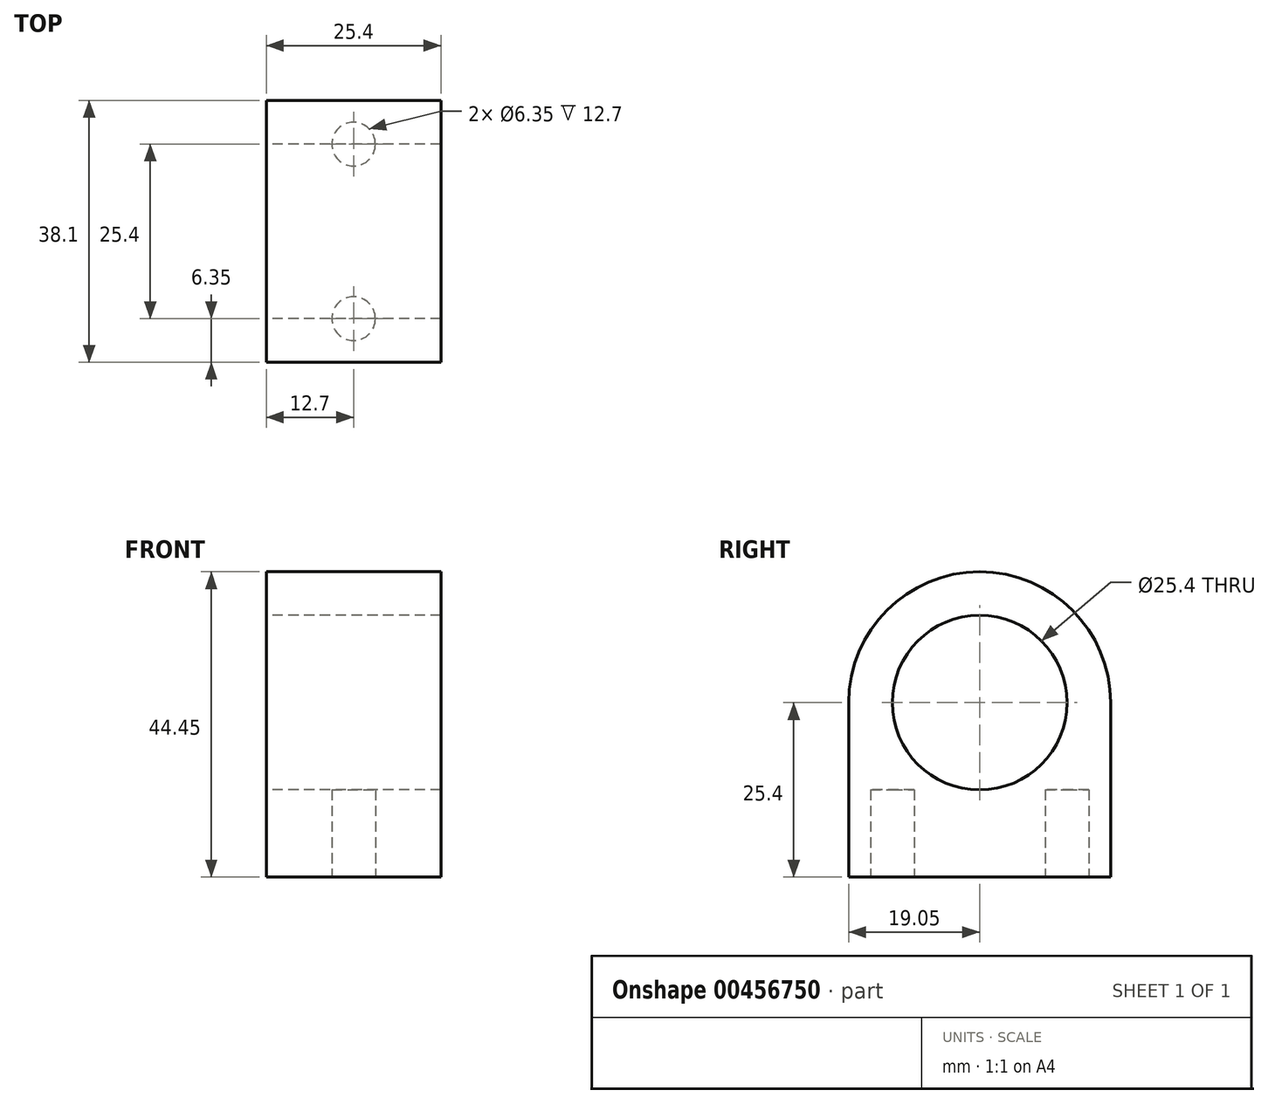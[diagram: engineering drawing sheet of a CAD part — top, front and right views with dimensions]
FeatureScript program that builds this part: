
annotation { "Feature Type Name" : "Feature", "Feature Type Description" : "" }
export const myFeature = defineFeature(function(context is Context, id is Id, definition is map)
    precondition{}
    {
        {
            var Q0;
            Q0=qCreatedBy(makeId("Right.planeOp"),FACE);
            var sketch = newSketch(context, id + "F0", { "sketchPlane" : qUnion([Q0])});
            skArc(sketch, "E0", {"start": v(19.05, 0) * mm, "mid": v(0, 19.05) * mm, "end": v(-19.05, 0) * mm});
            skCircle(sketch, "E1", {"center": v(0, 0) * mm, "radius": 12.7 * mm});
            skLineSegment(sketch, "E2", {"start": v(-19.05, 0) * mm, "end": v(-19.05, -25.4) * mm});
            skLineSegment(sketch, "E3", {"start": v(19.05, 0) * mm, "end": v(19.05, -25.4) * mm});
            skLineSegment(sketch, "E4", {"start": v(19.05, -25.4) * mm, "end": v(-19.05, -25.4) * mm});
            skSolve(sketch);
        }
        {
            var Q0;
            Q0=makeQuery(id+"F0.imprint","IMPRINT",FACE,{"disambiguationData":[TD([[makeQuery(id+"F0.imprint","IMPRINT",EDGE,{"derivedFrom":sQuery(id+"F0.wireOp",EDGE,"E0")}),1.0]])]});
            extrude(context, id + "F1", {"entities" : qUnion([Q0]), "depth" : 12.7 * mm, "hasSecondDirection" : true, "secondDirectionOppositeDirection" : true, "secondDirectionDepth" : 12.7 * mm});
        }
        {
            var Q0;
            Q0=makeQuery(id+"F1.opExtrude","SWEPT_FACE",FACE,{"disambiguationData":[OSD([sQuery(id+"F0.wireOp",EDGE,"E4")])]});
            var sketch = newSketch(context, id + "F2", { "sketchPlane" : qUnion([Q0])});
            skCircle(sketch, "E5", {"center": v(0, 12.7) * mm, "radius": 3.18 * mm});
            skCircle(sketch, "E6", {"center": v(0, -12.7) * mm, "radius": 3.18 * mm});
            skSolve(sketch);
        }
        {
            var Q0;
            Q0 = qSketchRegion(id + "F2", true);
            extrude(context, id + "F3", {"entities" : qUnion([Q0]), "operationType" : NewBodyOperationType.REMOVE, "oppositeDirection" : true, "depth" : 12.7 * mm});
        }
    });
